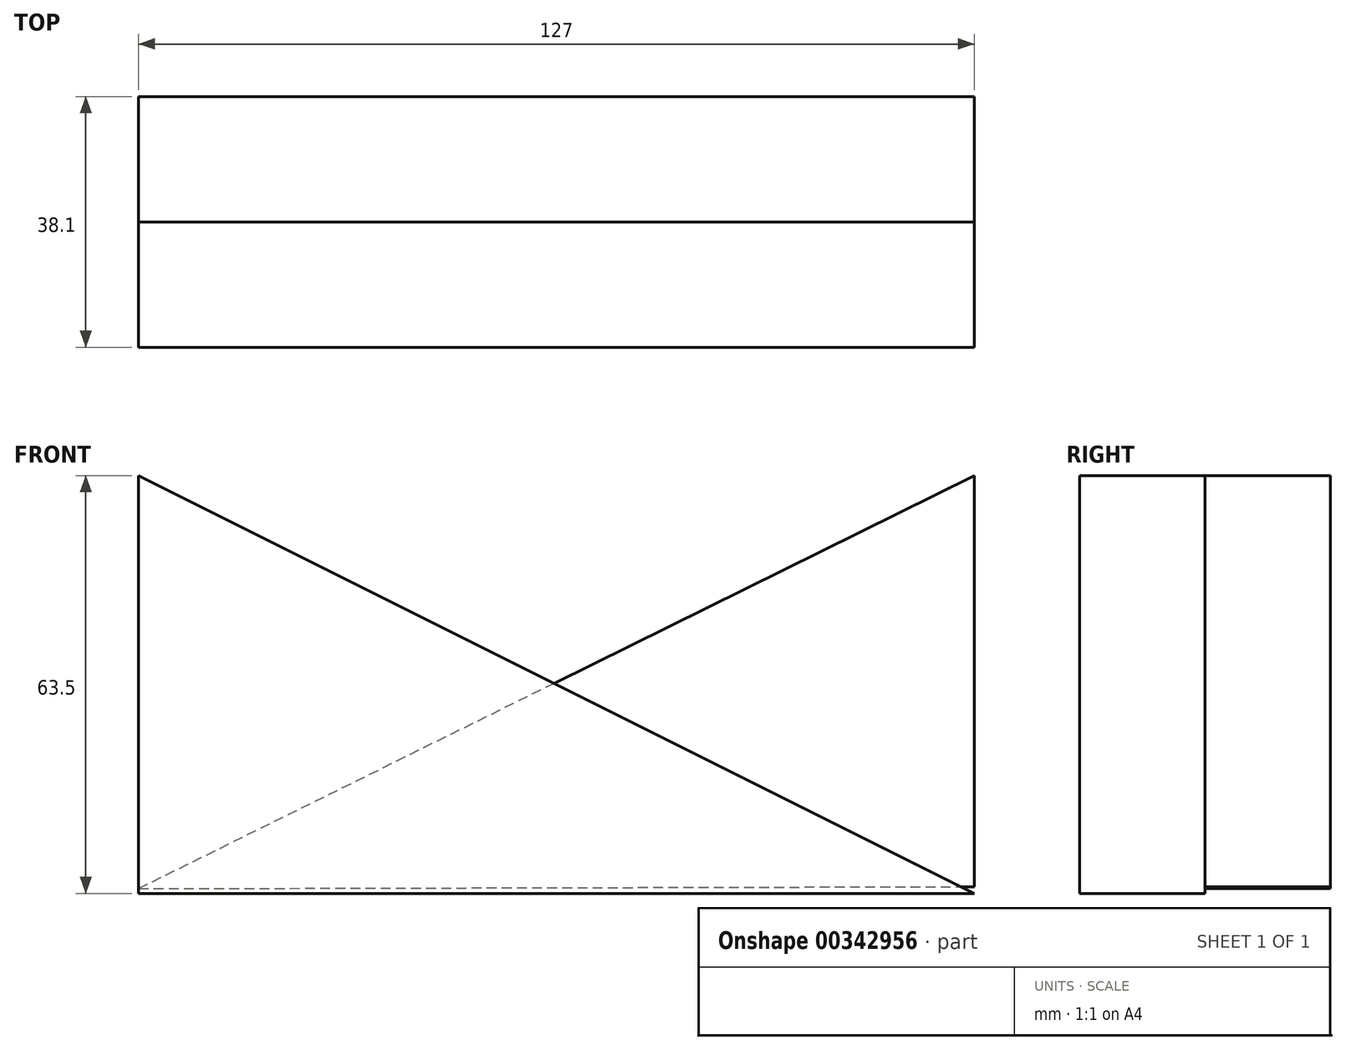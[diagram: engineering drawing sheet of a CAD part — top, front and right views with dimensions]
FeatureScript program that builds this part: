
annotation { "Feature Type Name" : "Feature", "Feature Type Description" : "" }
export const myFeature = defineFeature(function(context is Context, id is Id, definition is map)
    precondition{}
    {
        {
            var Q0;
            Q0=qCreatedBy(makeId("Front.planeOp"),FACE);
            var sketch = newSketch(context, id + "F0", { "sketchPlane" : qUnion([Q0])});
            skLineSegment(sketch, "E0", {"start": v(-60.34, 27.67) * mm, "end": v(-60.34, -35.83) * mm});
            skLineSegment(sketch, "E1", {"start": v(-60.34, -35.83) * mm, "end": v(66.66, -35.83) * mm});
            skLineSegment(sketch, "E2", {"start": v(-60.34, 27.67) * mm, "end": v(66.66, -35.83) * mm});
            skPoint(sketch, "E3.end.orphan", {"position": v(66.66, 27.67) * mm});
            skSolve(sketch);
        }
        {
            var Q0;
            Q0=makeQuery(id+"F0.imprint","IMPRINT",FACE,{"disambiguationData":[TD([[makeQuery(id+"F0.imprint","IMPRINT",EDGE,{"derivedFrom":sQuery(id+"F0.wireOp",EDGE,"E0")}),1.0]])]});
            extrude(context, id + "F1", {"entities" : qUnion([Q0]), "depth" : 19.05 * mm});
        }
        {
            var Q0;
            Q0=qCreatedBy(makeId("Front.planeOp"),FACE);
            var sketch = newSketch(context, id + "F2", { "sketchPlane" : qUnion([Q0])});
            skLineSegment(sketch, "E4", {"start": v(66.66, -34.8) * mm, "end": v(66.66, 28.7) * mm});
            skLineSegment(sketch, "E5", {"start": v(68.79, 28.7) * mm, "end": v(-60.34, -35.12) * mm});
            skLineSegment(sketch, "E6", {"start": v(-60.34, -35.12) * mm, "end": v(66.66, -34.8) * mm});
            skSolve(sketch);
        }
        {
            var Q0;
            {var subQ0=sQuery(id+"F2.wireOp",EDGE,"E6");Q0=makeQuery(id+"F2.imprint","IMPRINT",FACE,{"disambiguationData":[TD([[makeQuery(id+"F2.imprint","IMPRINT",EDGE,{"derivedFrom":subQ0}),1.0]])]});}
            extrude(context, id + "F3", {"entities" : qUnion([Q0]), "operationType" : NewBodyOperationType.ADD, "oppositeDirection" : true, "depth" : 19.05 * mm});
        }
    });
